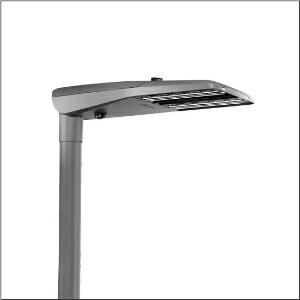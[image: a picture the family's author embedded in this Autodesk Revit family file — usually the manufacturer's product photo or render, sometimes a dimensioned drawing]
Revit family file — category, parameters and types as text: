
# Revit family: streetlight_sl_11_iq_midi___pc-r_5xc3f51y08me_63e7
name_source: partatom
category: Lighting Fixtures
units: mm (PartAtom-declared; Revit-internal decimal feet)

## family parameters
Cut with Voids When Loaded = No
Host = Face
Light Source = No
Part Type = Normal
Room Calculation Point = No
Round Connector Dimension = Use Diameter
Shared = No

## types (1)
- --- (1 x LED, 15540 lm, 122.7 W, 3000K)
    Apparent Load = 123 VA
    CIE Flux Codes = 37 73 96 100 100
    Color Rendering = 70
    Color Temperature = 3000K
    Default Elevation = 1800 mm
    Description = Streetlight SL 11 iQ midi, mast luminaire, primary light control with 3 zone facetted reflector, of plastic, silver coated, highly specular, primary optical cover: cover, of PMMA, transparent, light distribution: PC-R, light emission: direct distribution, primary light characteristic: asymmetric, right, installation type: post-top, side-entry, LED, High Power LED, rated luminous flux: 15.540lm, luminous efficacy: 127lm/W, light colour: 730, colour temperature: 3000K, control: presetting dimming logarithmic, Street-Remote, Auto-Match, Temp-Guard, Lumen-Switch, Night-Set, Smart-Wire, Light-Fading, Desk-Remote (wireless, voltage-free reading and setting of iQ features in the workshop via application-optimized NFC function/RFID function), optimised constant luminous flux control (CLO 2.0), with cable H07RN-F 5x 1.5mm², mains connection: 230..240V, AC, 50/60Hz, connection cable pre-assembled, cable length: 12,5m, start of lifetime: 123W, end of service life: 130W, reduction: 56W, luminaire housing, of diecast aluminium, powder-coated, Siteco® metallic grey (DB 702S), please order mast flange separately, inclination adjustable without tools: 0°, 5°, 10°, 15° (post-top) | 0°, -5°, -10°, -15° (side-entry), sealing non-destructively replaceable, multi-level sealing system, length: 780mm, width: 376mm, height: 118mm, mast flange for spigot size: 42mm (side-entry): 5XC10008XM4, 60/48mm (side-entry/post-top): 5XC10108XM2, 76/60mm (side-entry/post-top): 5XC10108XM1, equipment: Power, Smart Interface below and above, protection rating (complete): IP66, insulation class (complete): insulation class II (safety insulation), certification: CE, ENEC, VDE, UKCA, impact resistance: IK09, permissible operating ambient temperature for outdoor applications: -25..+50°C, standard-compliant lighting for roads and squares, Environmental Product Declaration (EPD) tested and certified by an independent institute, packaging unit: 1 piece

Light Distribution: PC-R
    Height = 118 mm
    Lamp = 1 x LED
    Lamp Light Flux = 15540 lm
    Lamp Power = 122.7 W
    Lamp count = 1
    Length = 780 mm
    Luminous efficacy = 127 lm/W
    Manufacturer = Siteco
    ModVariant = No
    Model = 5XC3F51Y08ME
    Number of Poles = 1
    OnlyDefault = Yes
    Power Factor = 1
    Product Name = Streetlight SL 11 iQ midi | PC-R
    Product group = mast luminaire | pylon top
    ProductGroupID = 6100
    Protection Class = Protection class II
    Protection Degree = IP 66
    RLX_Detail_Level = 1
    RLX_Emergency_Light_Flux = 0 lm
    RLX_Emergency_Type = 0
    RLX_Emergency_Type_DB = No
    RlxData = <blob elided: 73785 chars, md5=dfcae8a0>
    Socket = socket
    Standby Power = 0 W
    System Light Flux = 15540 lm
    System Power = 123 W
    Type Comments = factory setting: luminous flux: 100 % | dim-lin: 254 | 552 mA
    Type Image = l_1004429.jpg
    URL = http://relux.com
    VarID = @adj_082301
    Voltage = 0 V
    Weight = 0.00 kg
    Width = 376 mm

## geometry (parser evidence)
native form markers: Blend x4, Sweep x11
no freeform markers — native parametric forms only
